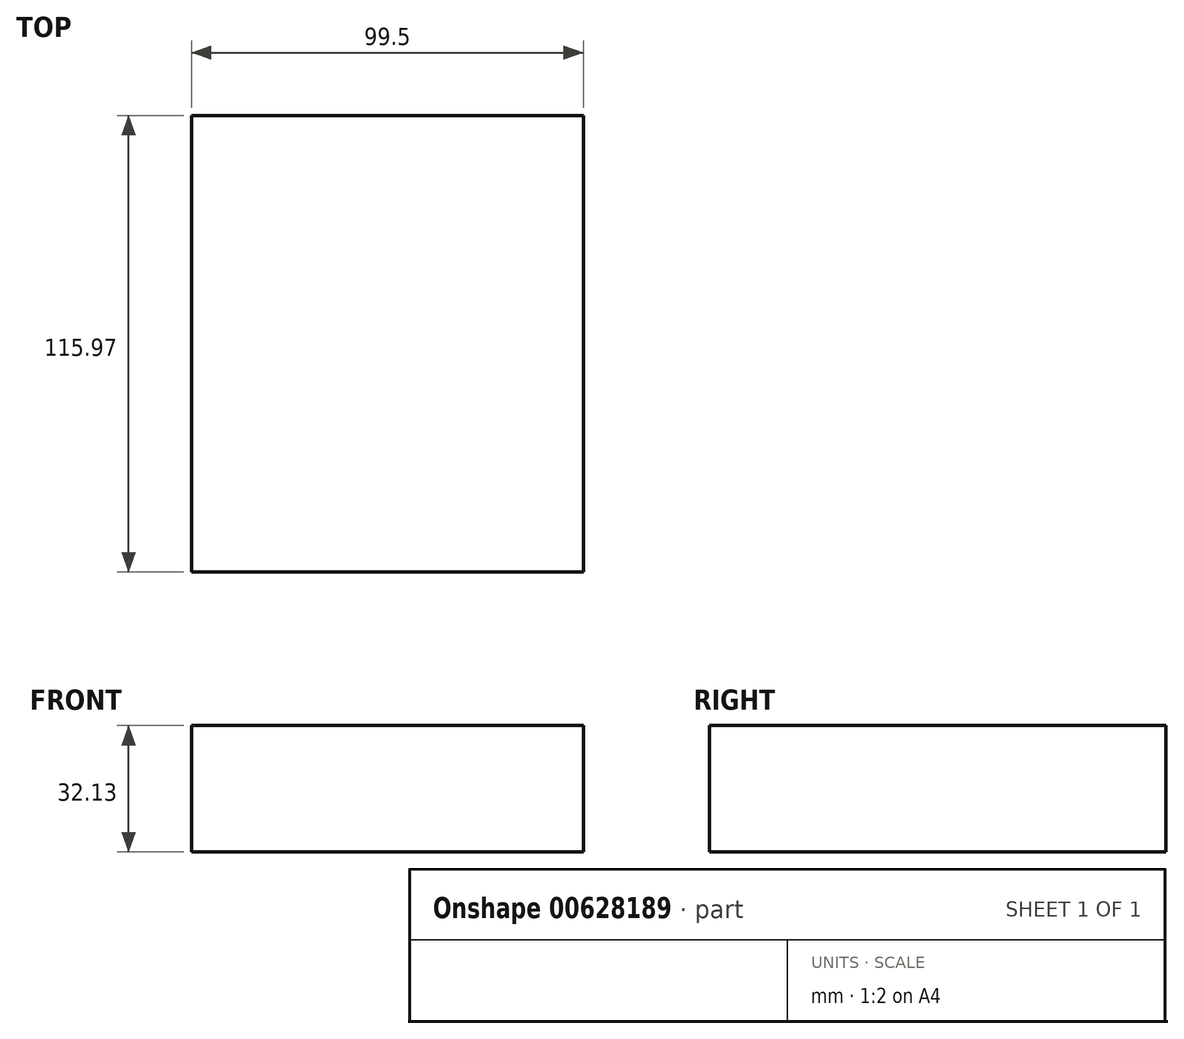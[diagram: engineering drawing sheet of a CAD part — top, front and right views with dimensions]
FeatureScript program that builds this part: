
annotation { "Feature Type Name" : "Feature", "Feature Type Description" : "" }
export const myFeature = defineFeature(function(context is Context, id is Id, definition is map)
    precondition{}
    {
        {
            var Q0;
            Q0=qCreatedBy(makeId("Top.planeOp"),FACE);
            var sketch = newSketch(context, id + "F0", { "sketchPlane" : qUnion([Q0])});
            skLineSegment(sketch, "E0", {"start": v(-48.64, 59.57) * mm, "end": v(-48.64, -56.4) * mm});
            skLineSegment(sketch, "E1", {"start": v(-48.64, -56.4) * mm, "end": v(50.86, -56.4) * mm});
            skLineSegment(sketch, "E2", {"start": v(50.86, -56.4) * mm, "end": v(50.86, 59.57) * mm});
            skLineSegment(sketch, "E3", {"start": v(50.86, 59.57) * mm, "end": v(-48.64, 59.57) * mm});
            skSolve(sketch);
        }
        {
            var Q0;
            Q0=makeQuery(id+"F0.imprint","IMPRINT",FACE,{"disambiguationData":[TD([[makeQuery(id+"F0.imprint","IMPRINT",EDGE,{"derivedFrom":sQuery(id+"F0.wireOp",EDGE,"E0")}),1.0]])]});
            extrude(context, id + "F1", {"entities" : qUnion([Q0]), "depth" : 32.13 * mm, "offsetDistance" : 25.4 * mm});
        }
    });
